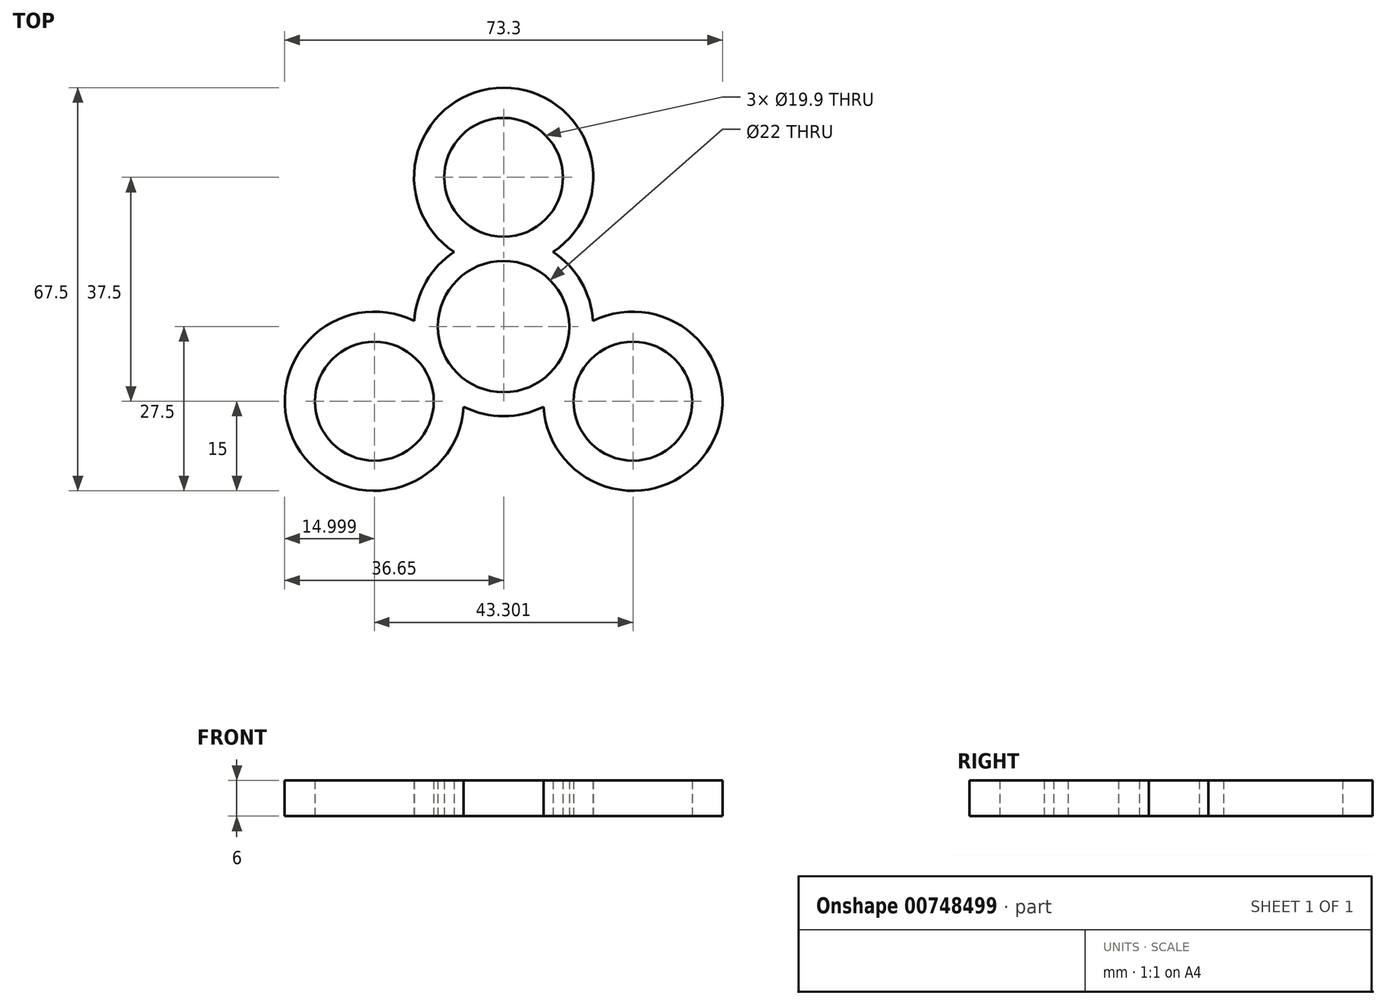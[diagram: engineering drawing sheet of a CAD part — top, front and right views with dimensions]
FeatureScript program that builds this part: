
annotation { "Feature Type Name" : "Feature", "Feature Type Description" : "" }
export const myFeature = defineFeature(function(context is Context, id is Id, definition is map)
    precondition{}
    {
        {
            var Q0;
            Q0=qCreatedBy(makeId("Top.planeOp"),FACE);
            var sketch = newSketch(context, id + "F0", { "sketchPlane" : qUnion([Q0])});
            skCircle(sketch, "E0", {"center": v(0, 0) * mm, "radius": 11 * mm});
            skArc(sketch, "E1", {"start": v(-8.3, 12.5) * mm, "mid": v(-13, 7.5) * mm, "end": v(-14.97, 0.93) * mm});
            skLineSegment(sketch, "E2", {"start": v(0, 0) * mm, "end": v(0, 25) * mm});
            skArc(sketch, "E3", {"start": v(8.3, 12.5) * mm, "mid": v(0, 40) * mm, "end": v(-8.3, 12.5) * mm});
            skCircle(sketch, "E4", {"center": v(0, 25) * mm, "radius": 9.95 * mm});
            skCircle(sketch, "E5.1.0", {"center": v(-21.65, -12.5) * mm, "radius": 9.95 * mm});
            skArc(sketch, "E5.1.1", {"start": v(-14.97, 0.93) * mm, "mid": v(-34.64, -20) * mm, "end": v(-6.68, -13.43) * mm});
            skCircle(sketch, "E5.2.0", {"center": v(21.65, -12.5) * mm, "radius": 9.95 * mm});
            skArc(sketch, "E5.2.1", {"start": v(6.68, -13.43) * mm, "mid": v(34.64, -20) * mm, "end": v(14.97, 0.93) * mm});
            skArc(sketch, "E6.trimOffspring", {"start": v(-6.68, -13.43) * mm, "mid": v(0, -15) * mm, "end": v(6.68, -13.43) * mm});
            skArc(sketch, "E7.trimOffspring", {"start": v(14.97, 0.93) * mm, "mid": v(13, 7.5) * mm, "end": v(8.3, 12.5) * mm});
            skSolve(sketch);
        }
        {
            var Q0;
            Q0 = qSketchRegion(id + "F0", true);
            extrude(context, id + "F1", {"entities" : qUnion([Q0]), "depth" : 6 * mm, "offsetDistance" : 25 * mm});
        }
    });
